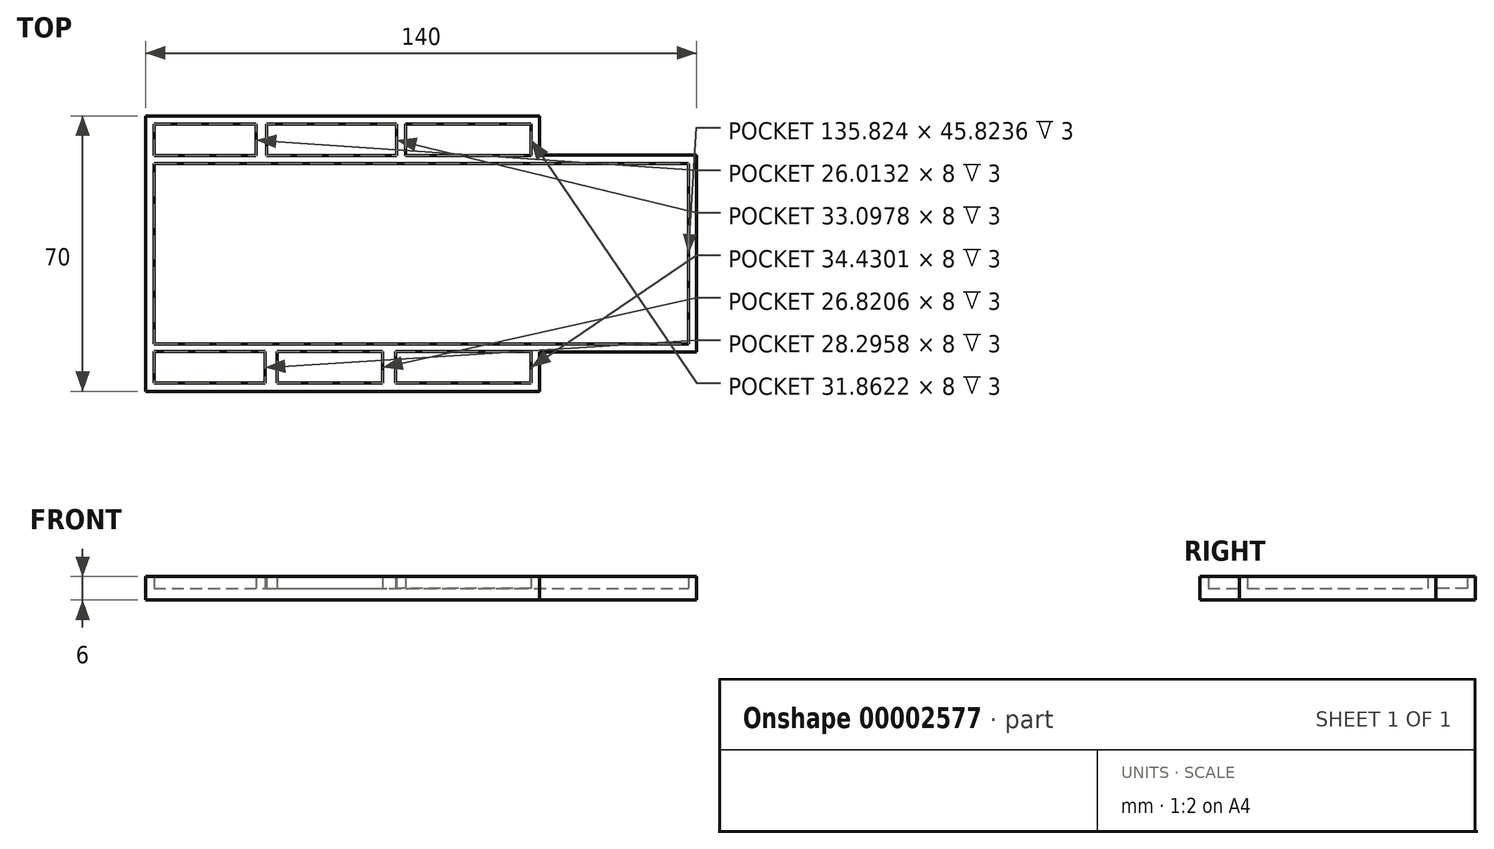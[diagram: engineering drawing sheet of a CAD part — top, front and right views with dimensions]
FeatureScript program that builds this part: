
annotation { "Feature Type Name" : "Feature", "Feature Type Description" : "" }
export const myFeature = defineFeature(function(context is Context, id is Id, definition is map)
    precondition{}
    {
        {
            var Q0;
            Q0=qCreatedBy(makeId("Top.planeOp"),FACE);
            var sketch = newSketch(context, id + "F0", { "sketchPlane" : qUnion([Q0])});
            skLineSegment(sketch, "E0", {"start": v(-96.96, -38.59) * mm, "end": v(-96.96, 31.41) * mm});
            skLineSegment(sketch, "E1", {"start": v(-96.96, 31.41) * mm, "end": v(3.04, 31.41) * mm});
            skLineSegment(sketch, "E2", {"start": v(3.04, 31.41) * mm, "end": v(3.04, 21.41) * mm});
            skLineSegment(sketch, "E3", {"start": v(3.04, 21.41) * mm, "end": v(43.04, 21.41) * mm});
            skLineSegment(sketch, "E4", {"start": v(-96.96, -38.59) * mm, "end": v(3.04, -38.59) * mm});
            skLineSegment(sketch, "E5", {"start": v(3.04, -38.59) * mm, "end": v(3.04, -28.59) * mm});
            skLineSegment(sketch, "E6", {"start": v(3.04, -28.59) * mm, "end": v(43.04, -28.59) * mm});
            skLineSegment(sketch, "E7", {"start": v(43.04, -28.59) * mm, "end": v(43.04, 21.41) * mm});
            skSolve(sketch);
        }
        {
            var Q0;
            Q0=makeQuery(id+"F0.imprint","IMPRINT",FACE,{"disambiguationData":[TD([[makeQuery(id+"F0.imprint","IMPRINT",EDGE,{"derivedFrom":sQuery(id+"F0.wireOp",EDGE,"E0")}),-1.0]])]});
            extrude(context, id + "F1", {"entities" : qUnion([Q0]), "depth" : 3 * mm});
        }
        {
            var Q0;
            Q0=makeQuery(id+"F1.opExtrude","CAP_FACE",FACE,{"disambiguationData":[OSD([sQuery(id+"F0.wireOp",EDGE,"E0"),sQuery(id+"F0.wireOp",EDGE,"E1"),sQuery(id+"F0.wireOp",EDGE,"E2"),sQuery(id+"F0.wireOp",EDGE,"E3"),sQuery(id+"F0.wireOp",EDGE,"E4"),sQuery(id+"F0.wireOp",EDGE,"E5"),sQuery(id+"F0.wireOp",EDGE,"E6"),sQuery(id+"F0.wireOp",EDGE,"E7")])],"isStart":false});
            var sketch = newSketch(context, id + "F2", { "sketchPlane" : qUnion([Q0])});
            skLineSegment(sketch, "E8.0", {"start": v(-94.87, -36.5) * mm, "end": v(0.95, -36.5) * mm});
            skLineSegment(sketch, "E8.1", {"start": v(0.95, -36.5) * mm, "end": v(0.95, -26.5) * mm});
            skLineSegment(sketch, "E8.2", {"start": v(0.95, -26.5) * mm, "end": v(40.95, -26.5) * mm});
            skLineSegment(sketch, "E8.3", {"start": v(40.95, -26.5) * mm, "end": v(40.95, 19.32) * mm});
            skLineSegment(sketch, "E8.4", {"start": v(0.95, 19.32) * mm, "end": v(40.95, 19.32) * mm});
            skLineSegment(sketch, "E8.5", {"start": v(-94.87, -36.5) * mm, "end": v(-94.87, 29.32) * mm});
            skLineSegment(sketch, "E8.6", {"start": v(0.95, 29.32) * mm, "end": v(0.95, 19.32) * mm});
            skLineSegment(sketch, "E8.7", {"start": v(-94.87, 29.32) * mm, "end": v(0.95, 29.32) * mm});
            skSolve(sketch);
        }
        {
            var Q0;
            Q0=makeQuery(id+"F2.imprint","IMPRINT",FACE,{"disambiguationData":[TD([[makeQuery(id+"F2.imprint","IMPRINT",EDGE,{"derivedFrom":sQuery(id+"F2.wireOp",EDGE,"E8.0")}),-1.0]])]});
            extrude(context, id + "F3", {"entities" : qUnion([Q0]), "operationType" : NewBodyOperationType.ADD, "depth" : 3 * mm});
        }
        {
            var Q0;
            Q0=makeQuery(id+"F1.opExtrude","CAP_FACE",FACE,{"disambiguationData":[OSD([sQuery(id+"F0.wireOp",EDGE,"E0"),sQuery(id+"F0.wireOp",EDGE,"E1"),sQuery(id+"F0.wireOp",EDGE,"E2"),sQuery(id+"F0.wireOp",EDGE,"E3"),sQuery(id+"F0.wireOp",EDGE,"E4"),sQuery(id+"F0.wireOp",EDGE,"E5"),sQuery(id+"F0.wireOp",EDGE,"E6"),sQuery(id+"F0.wireOp",EDGE,"E7")])],"isStart":false});
            var sketch = newSketch(context, id + "F4", { "sketchPlane" : qUnion([Q0])});
            skLineSegment(sketch, "E9.bottom", {"start": v(0.95, -26.5) * mm, "end": v(-94.87, -26.5) * mm});
            skLineSegment(sketch, "E9.top", {"start": v(0.95, -28.5) * mm, "end": v(-33.48, -28.5) * mm});
            skLineSegment(sketch, "E9.left", {"start": v(0.95, -26.5) * mm, "end": v(0.95, -28.5) * mm});
            skLineSegment(sketch, "E9.right", {"start": v(-94.87, -26.5) * mm, "end": v(-94.87, -28.5) * mm});
            skLineSegment(sketch, "E10.bottom", {"start": v(0.95, 19.32) * mm, "end": v(-94.87, 19.32) * mm});
            skLineSegment(sketch, "E10.top", {"start": v(0.95, 21.32) * mm, "end": v(-30.9, 21.32) * mm});
            skLineSegment(sketch, "E10.left", {"start": v(0.95, 19.32) * mm, "end": v(0.95, 21.32) * mm});
            skLineSegment(sketch, "E10.right", {"start": v(-94.87, 19.32) * mm, "end": v(-94.87, 21.32) * mm});
            skLineSegment(sketch, "E11.top", {"start": v(-68.86, 29.32) * mm, "end": v(-66.3, 29.32) * mm});
            skLineSegment(sketch, "E11.left", {"start": v(-68.86, 21.32) * mm, "end": v(-68.86, 29.32) * mm});
            skLineSegment(sketch, "E11.right", {"start": v(-66.3, 21.32) * mm, "end": v(-66.3, 29.32) * mm});
            skLineSegment(sketch, "E12.top", {"start": v(-33.2, 29.32) * mm, "end": v(-30.9, 29.32) * mm});
            skLineSegment(sketch, "E12.left", {"start": v(-33.2, 21.32) * mm, "end": v(-33.2, 29.32) * mm});
            skLineSegment(sketch, "E12.right", {"start": v(-30.9, 21.32) * mm, "end": v(-30.9, 29.32) * mm});
            skLineSegment(sketch, "E13.top", {"start": v(-66.58, -36.5) * mm, "end": v(-63.58, -36.5) * mm});
            skLineSegment(sketch, "E13.left", {"start": v(-66.58, -28.5) * mm, "end": v(-66.58, -36.5) * mm});
            skLineSegment(sketch, "E13.right", {"start": v(-63.58, -28.5) * mm, "end": v(-63.58, -36.5) * mm});
            skLineSegment(sketch, "E14.top", {"start": v(-36.76, -36.5) * mm, "end": v(-33.48, -36.5) * mm});
            skLineSegment(sketch, "E14.left", {"start": v(-36.76, -28.5) * mm, "end": v(-36.76, -36.5) * mm});
            skLineSegment(sketch, "E14.right", {"start": v(-33.48, -28.5) * mm, "end": v(-33.48, -36.5) * mm});
            skLineSegment(sketch, "E15.trimOffspring", {"start": v(-68.86, 21.32) * mm, "end": v(-94.87, 21.32) * mm});
            skLineSegment(sketch, "E16.trimOffspring", {"start": v(-33.2, 21.32) * mm, "end": v(-66.3, 21.32) * mm});
            skLineSegment(sketch, "E17.trimOffspring", {"start": v(-36.76, -28.5) * mm, "end": v(-63.58, -28.5) * mm});
            skLineSegment(sketch, "E18.trimOffspring", {"start": v(-66.58, -28.5) * mm, "end": v(-94.87, -28.5) * mm});
            skSolve(sketch);
        }
        {
            var Q0;
            Q0=makeQuery(id+"F4.imprint","IMPRINT",FACE,{"disambiguationData":[TD([[makeQuery(id+"F4.imprint","IMPRINT",EDGE,{"derivedFrom":sQuery(id+"F4.wireOp",EDGE,"E9.bottom")}),1.0]])]});
            var Q1;
            Q1=makeQuery(id+"F4.imprint","IMPRINT",FACE,{"disambiguationData":[TD([[makeQuery(id+"F4.imprint","IMPRINT",EDGE,{"derivedFrom":sQuery(id+"F4.wireOp",EDGE,"E10.bottom")}),-1.0]])]});
            extrude(context, id + "F5", {"entities" : qUnion([Q0, Q1]), "operationType" : NewBodyOperationType.ADD, "depth" : 3 * mm});
        }
    });
